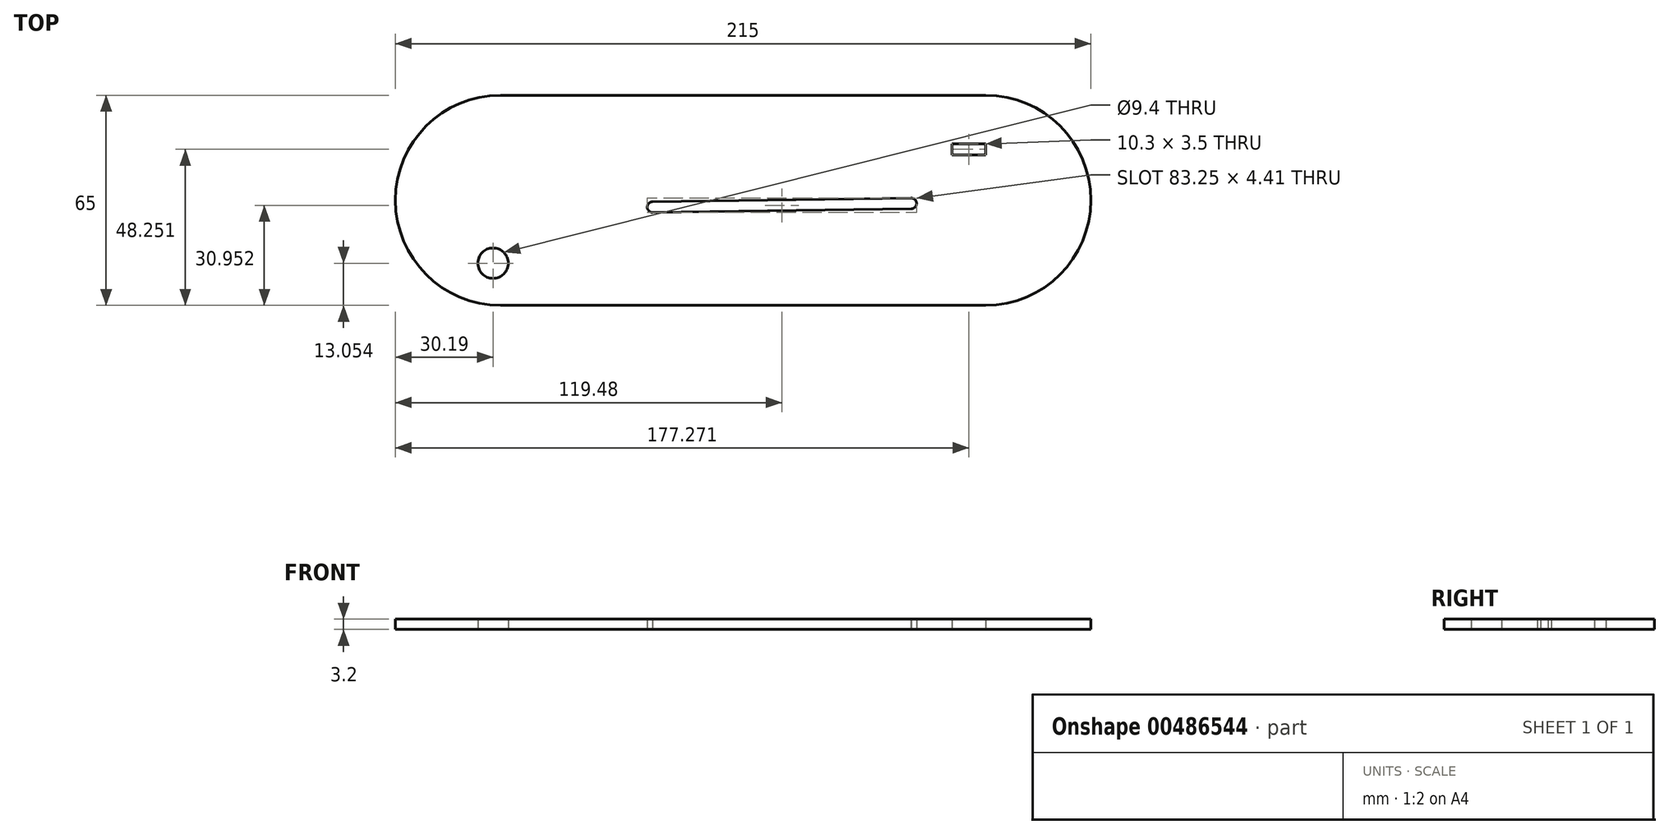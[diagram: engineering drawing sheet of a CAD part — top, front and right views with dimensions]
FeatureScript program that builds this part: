
annotation { "Feature Type Name" : "Feature", "Feature Type Description" : "" }
export const myFeature = defineFeature(function(context is Context, id is Id, definition is map)
    precondition{}
    {
        {
            var Q0;
            Q0=qCreatedBy(makeId("Top.planeOp"),FACE);
            var sketch = newSketch(context, id + "F0", { "sketchPlane" : qUnion([Q0])});
            skLineSegment(sketch, "E0", {"start": v(-72.27, 61.2) * mm, "end": v(77.73, 61.2) * mm});
            skLineSegment(sketch, "E1", {"start": v(-72.27, -3.8) * mm, "end": v(77.73, -3.8) * mm});
            skArc(sketch, "E2", {"start": v(-72.27, 61.2) * mm, "mid": v(-104.77, 28.7) * mm, "end": v(-72.27, -3.8) * mm});
            skArc(sketch, "E3", {"start": v(77.73, -3.8) * mm, "mid": v(110.23, 28.7) * mm, "end": v(77.73, 61.2) * mm});
            skCircle(sketch, "E4", {"center": v(-74.58, 9.25) * mm, "radius": 4.7 * mm});
            skCircle(sketch, "E5", {"center": v(54.69, 27.71) * mm, "radius": 1.65 * mm});
            skLineSegment(sketch, "E6", {"start": v(54.57, 29.36) * mm, "end": v(-25.27, 28.25) * mm});
            skLineSegment(sketch, "E7", {"start": v(-25.27, 24.95) * mm, "end": v(54.74, 26.06) * mm});
            skCircle(sketch, "E8", {"center": v(-25.27, 26.6) * mm, "radius": 1.65 * mm});
            skLineSegment(sketch, "E9.bottom", {"start": v(67.35, 46.2) * mm, "end": v(77.65, 46.2) * mm});
            skLineSegment(sketch, "E9.top", {"start": v(67.35, 42.7) * mm, "end": v(77.65, 42.7) * mm});
            skLineSegment(sketch, "E9.left", {"start": v(67.35, 46.2) * mm, "end": v(67.35, 42.7) * mm});
            skLineSegment(sketch, "E9.right", {"start": v(77.65, 46.2) * mm, "end": v(77.65, 42.7) * mm});
            skPoint(sketch, "E9.middle", {"position": v(72.5, 44.45) * mm});
            skSolve(sketch);
        }
        {
            var Q0;
            Q0=makeQuery(id+"F0.imprint","IMPRINT",FACE,{"disambiguationData":[TD([[makeQuery(id+"F0.imprint","IMPRINT",EDGE,{"derivedFrom":sQuery(id+"F0.wireOp",EDGE,"E0")}),-1.0]])]});
            extrude(context, id + "F1", {"entities" : qUnion([Q0]), "depth" : 3.2 * mm, "offsetDistance" : 25 * mm});
        }
    });
